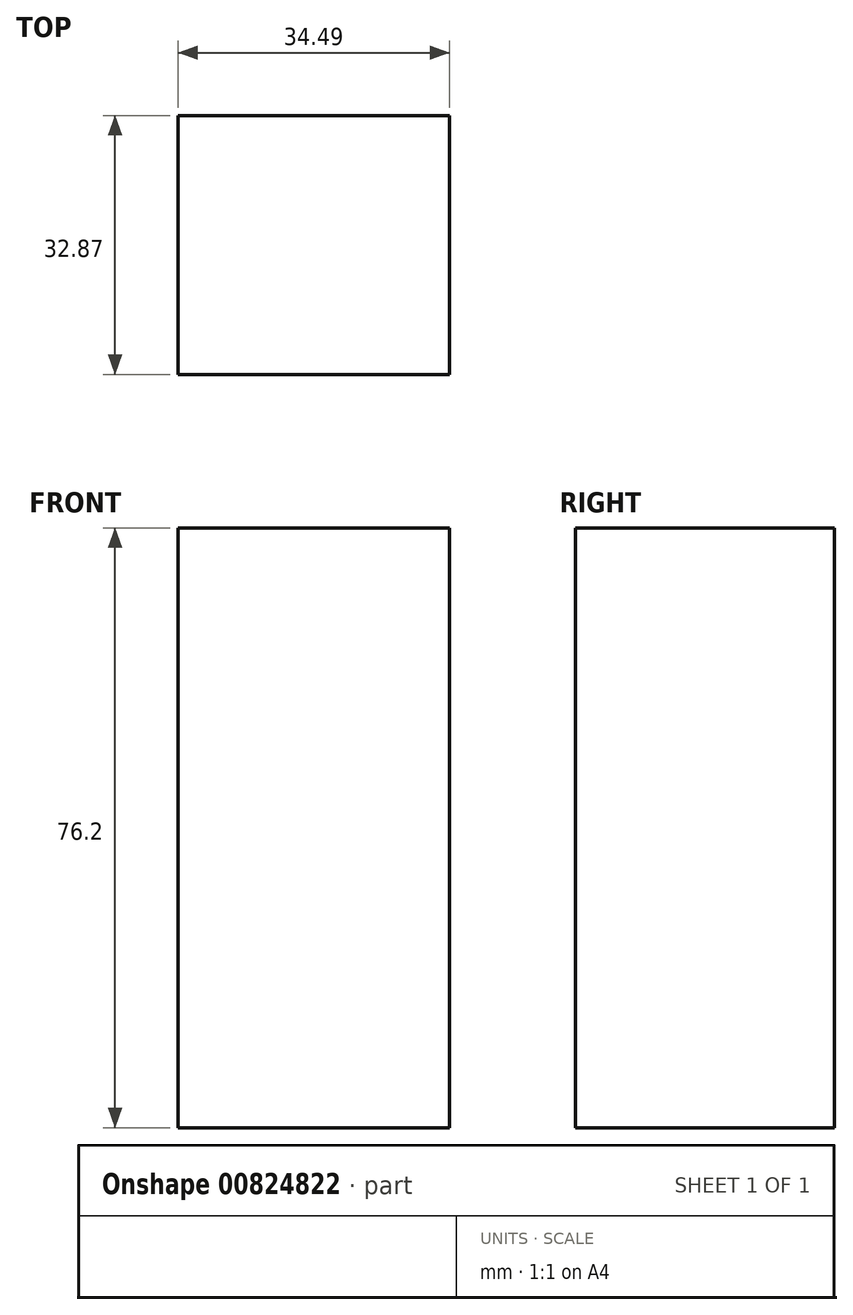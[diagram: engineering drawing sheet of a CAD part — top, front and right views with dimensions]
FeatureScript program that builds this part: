
annotation { "Feature Type Name" : "Feature", "Feature Type Description" : "" }
export const myFeature = defineFeature(function(context is Context, id is Id, definition is map)
    precondition{}
    {
        {
            var Q0;
            Q0=qCreatedBy(makeId("Top.planeOp"),FACE);
            var sketch = newSketch(context, id + "F0", { "sketchPlane" : qUnion([Q0])});
            skLineSegment(sketch, "E0.bottom", {"start": v(0, 0) * mm, "end": v(34.49, 0) * mm});
            skLineSegment(sketch, "E0.top", {"start": v(0, 32.87) * mm, "end": v(34.49, 32.87) * mm});
            skLineSegment(sketch, "E0.left", {"start": v(0, 0) * mm, "end": v(0, 32.87) * mm});
            skLineSegment(sketch, "E0.right", {"start": v(34.49, 0) * mm, "end": v(34.49, 32.87) * mm});
            skSolve(sketch);
        }
        {
            var Q0;
            Q0 = qSketchRegion(id + "F0", true);
            extrude(context, id + "F1", {"entities" : qUnion([Q0]), "depth" : 76.2 * mm, "offsetDistance" : 25.4 * mm});
        }
    });
